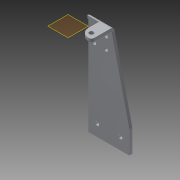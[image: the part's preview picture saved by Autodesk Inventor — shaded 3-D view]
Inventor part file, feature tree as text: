
AUTODESK INVENTOR PART (.ipt)
format: ipt  version: 2014 (Build 180170000, 170)  size: 166,400 bytes
history: native  units: in
note: dims shown in document units (in); Inventor stores cm internally (conversion verified against a paired STEP export)
features: other x4, sheet_metal_op x1, plane x1, fillet x1, sketch x1
ambient origin geometry x8: Origin, YZ Plane, XZ Plane, XY Plane, X Axis, Y Axis, Z Axis, Center Point
bodies: Solid1 (feature_tree)
feature tree (8):
  sheet_metal_op  "Face1"
  plane  "Work Plane1"
  fillet  "Fillet5"  Radius=0.163in
  sketch  "Sketch1"  dims[d4=0.7874in d6=1.0in d7=0.3937in d9=1.0in d11=0.0625in d22=0.5in d28=0.187in d29=0.25in d34=0.75in d47=0.125in d48=0.25in d49=0.25in d50=0.375in d51=0.0625in d52=0.0in d54=1.0in d55=4.1875in d56=1.0in d57=1.75in d58=0.375in d80=0.5in d81=0.25in d82=0.25in d83=0.7874in d85=0.5in d86=0.7874in d88=0.5in d0=0.125in d1=0.125in d3=0.0in]
  other  "Plate1"
  other  "Cut3"
  other  "Definition1"
  other  "Cut1"
